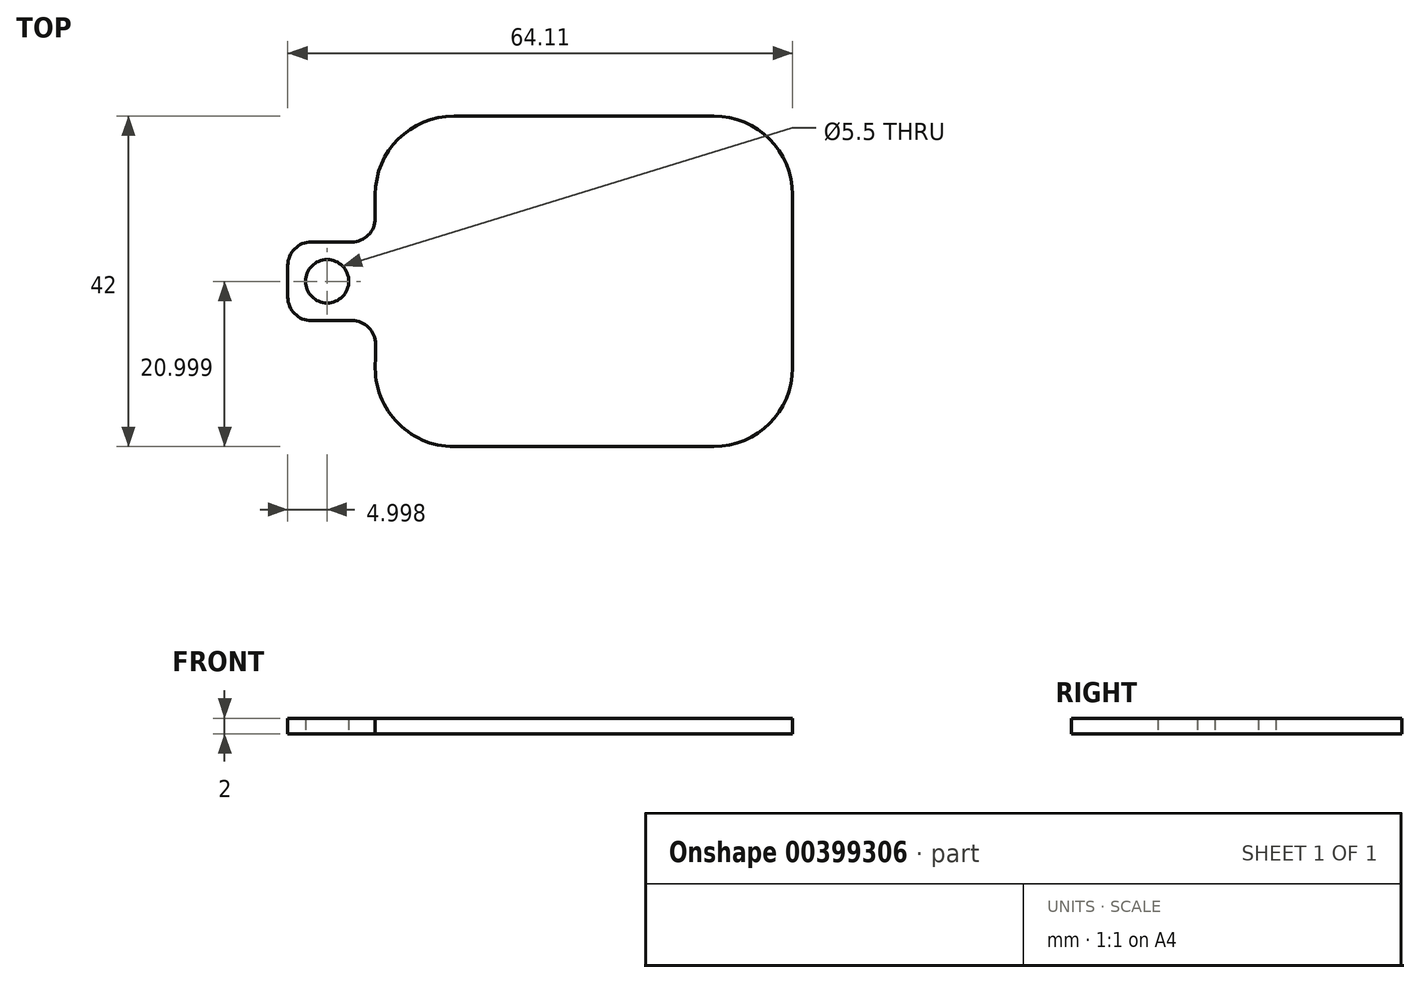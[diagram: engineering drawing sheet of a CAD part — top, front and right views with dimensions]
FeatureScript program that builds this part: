
annotation { "Feature Type Name" : "Feature", "Feature Type Description" : "" }
export const myFeature = defineFeature(function(context is Context, id is Id, definition is map)
    precondition{}
    {
        {
            var Q0;
            Q0=qCreatedBy(makeId("Top.planeOp"),FACE);
            var sketch = newSketch(context, id + "F0", { "sketchPlane" : qUnion([Q0])});
            skLineSegment(sketch, "E0.bottom", {"start": v(2, -20.44) * mm, "end": v(35, -20.44) * mm});
            skLineSegment(sketch, "E0.top", {"start": v(2, 21.56) * mm, "end": v(35, 21.56) * mm});
            skLineSegment(sketch, "E0.left", {"start": v(-8, 8.56) * mm, "end": v(-8, 11.56) * mm});
            skLineSegment(sketch, "E0.right", {"start": v(45, -10.44) * mm, "end": v(45, 11.56) * mm});
            skPoint(sketch, "E1.visualSharp", {"position": v(-8, 21.56) * mm});
            skArc(sketch, "E1.filletArc", {"start": v(2, 21.56) * mm, "mid": v(-5.07, 18.63) * mm, "end": v(-8, 11.56) * mm});
            skPoint(sketch, "E2.visualSharp", {"position": v(45, 21.56) * mm});
            skArc(sketch, "E2.filletArc", {"start": v(45, 11.56) * mm, "mid": v(42.07, 18.63) * mm, "end": v(35, 21.56) * mm});
            skPoint(sketch, "E3.visualSharp", {"position": v(45, -20.44) * mm});
            skArc(sketch, "E3.filletArc", {"start": v(35, -20.44) * mm, "mid": v(42.07, -17.51) * mm, "end": v(45, -10.44) * mm});
            skPoint(sketch, "E4.visualSharp", {"position": v(-8, -20.44) * mm});
            skArc(sketch, "E4.filletArc", {"start": v(-7.95, -9.44) * mm, "mid": v(-5.42, -17.15) * mm, "end": v(2, -20.44) * mm});
            skPoint(sketch, "E5.endSnap0", {"position": v(-8, 0.56) * mm});
            skLineSegment(sketch, "E6.0", {"start": v(-11, 5.56) * mm, "end": v(-16.11, 5.56) * mm});
            skLineSegment(sketch, "E7.0", {"start": v(-10.95, -4.44) * mm, "end": v(-16.11, -4.44) * mm});
            skLineSegment(sketch, "E8", {"start": v(-19.11, 2.56) * mm, "end": v(-19.11, -1.44) * mm});
            skPoint(sketch, "E9.visualSharp", {"position": v(-19.11, 5.56) * mm});
            skArc(sketch, "E9.filletArc", {"start": v(-16.11, 5.56) * mm, "mid": v(-18.23, 4.68) * mm, "end": v(-19.11, 2.56) * mm});
            skPoint(sketch, "E10.visualSharp", {"position": v(-19.11, -4.44) * mm});
            skArc(sketch, "E10.filletArc", {"start": v(-19.11, -1.44) * mm, "mid": v(-18.23, -3.56) * mm, "end": v(-16.11, -4.44) * mm});
            skPoint(sketch, "E11.centerSnap0", {"position": v(-19.11, 0.56) * mm});
            skPoint(sketch, "E12.newPointB", {"position": v(-8, -10.44) * mm});
            skArc(sketch, "E12.filletArc", {"start": v(-11, 5.56) * mm, "mid": v(-8.88, 6.44) * mm, "end": v(-8, 8.56) * mm});
            skLineSegment(sketch, "E13", {"start": v(-7.95, -9.44) * mm, "end": v(-7.95, -7.44) * mm});
            skPoint(sketch, "E14.visualSharp", {"position": v(-7.95, -4.44) * mm});
            skArc(sketch, "E14.filletArc", {"start": v(-7.95, -7.44) * mm, "mid": v(-8.83, -5.32) * mm, "end": v(-10.95, -4.44) * mm});
            skCircle(sketch, "E15", {"center": v(-14.11, 0.56) * mm, "radius": 2.75 * mm});
            skSolve(sketch);
        }
        {
            var Q0;
            Q0=makeQuery(id+"F0.imprint","IMPRINT",FACE,{"disambiguationData":[TD([[makeQuery(id+"F0.imprint","IMPRINT",EDGE,{"derivedFrom":sQuery(id+"F0.wireOp",EDGE,"E0.bottom")}),1.0]])]});
            extrude(context, id + "F1", {"entities" : qUnion([Q0]), "depth" : 2 * mm});
        }
    });
